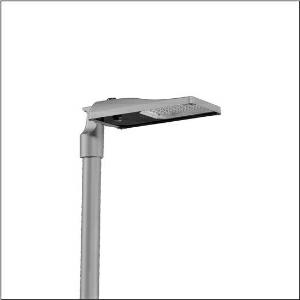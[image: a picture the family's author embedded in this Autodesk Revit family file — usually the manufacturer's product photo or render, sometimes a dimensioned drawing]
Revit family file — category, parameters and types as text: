
# Revit family: streetlight_sl_31_mini___p0_8a_5xh6u31t08ha_cf92
name_source: partatom
category: Lighting Fixtures
units: mm (PartAtom-declared; Revit-internal decimal feet)

## family parameters
Cut with Voids When Loaded = No
Host = Face
Light Source = No
Part Type = Normal
Room Calculation Point = No
Round Connector Dimension = Use Diameter
Shared = No

## types (1)
- --- (1 x LED, 9320 lm, 68.3 W, 3000K)
    Apparent Load = 68 VA
    CIE Flux Codes = 33 69 96 100 100
    Color Rendering = 70
    Color Temperature = 3000K
    Default Elevation = 1800 mm
    Description = Streetlight SL 31 mini D4i, Desk-Remote mast luminaire for post-top, side-entry; light control with lens of PMMA; light distribution: P0.8a, direct asymmetric distribution, for standard-compliant lighting for roads and squares; LED: luminous flux: 9.320lm, light colour: 730, colour temperature: 3000K; luminous efficacy: 136,7lm/W; control: pre-setting: logarithmic dimming characteristic, flexible luminous flux parameterisation, time-dependent luminous flux control, constant luminous flux control, power reduction, intelligent temperature release in ECG and LED module, overheat protection; luminaire housing, of diecast aluminium, Siteco® metallic grey (DB 702S), corrosivity category C5 high according to DIN EN ISO 12944; cover of toughened safety glass, transparent, opened without tools; mast flange of diecast aluminium, Siteco® metallic grey (DB 702S), spigot size: 76/60mm, mast flange included unmounted; with cable H07RN-F 2x 1.5mm², cable length: 8,5m, connection cable pre-assembled; mains connection: 220..240V, AC, 50/60Hz; power consumption (at start of service life): 68,2W / (at end of service life): 74,4W / (with reduced operation 50%): 29,7W; protection rating (complete): IP66; insulation class (complete): insulation class II (safety insulation); impact resistance: IK09; certification: CE, ENEC, ENEC+, VDE, UKCA, ZD4i; permissible operating ambient temperature for outdoor applications: -40..+50°C; packaging unit: 1 piece

Light Distribution: P0.8a
    Height = 76 mm
    Lamp = 1 x LED
    Lamp Light Flux = 9320 lm
    Lamp Power = 68.3 W
    Lamp count = 1
    Length = 547 mm
    Luminous efficacy = 136 lm/W
    Manufacturer = Siteco
    ModVariant = No
    Model = 5XH6U31T08HA
    Number of Poles = 1
    OnlyDefault = Yes
    Power Factor = 1
    Product Name = Streetlight SL 31 mini | P0.8a
    Product group = mast luminaire | pylon top
    ProductGroupID = 6100
    Protection Class = Protection class II
    Protection Degree = IP 66
    RLX_Detail_Level = 1
    RLX_Emergency_Light_Flux = 0 lm
    RLX_Emergency_Type = 0
    RLX_Emergency_Type_DB = No
    RlxData = <blob elided: 24141 chars, md5=4a3e2765>
    Socket = socket
    Standby Power = 0 W
    System Light Flux = 9320 lm
    System Power = 68 W
    Type Comments = factory setting: luminous flux: 100 % | dim-lin: 254 | 692 mA
    Type Image = l_1300332.jpg
    URL = http://relux.com
    VarID = @adj_003303
    Voltage = 0 V
    Weight = 0.00 kg
    Width = 265 mm

## geometry (parser evidence)
native form markers: Blend x4, Sweep x12
no freeform markers — native parametric forms only
